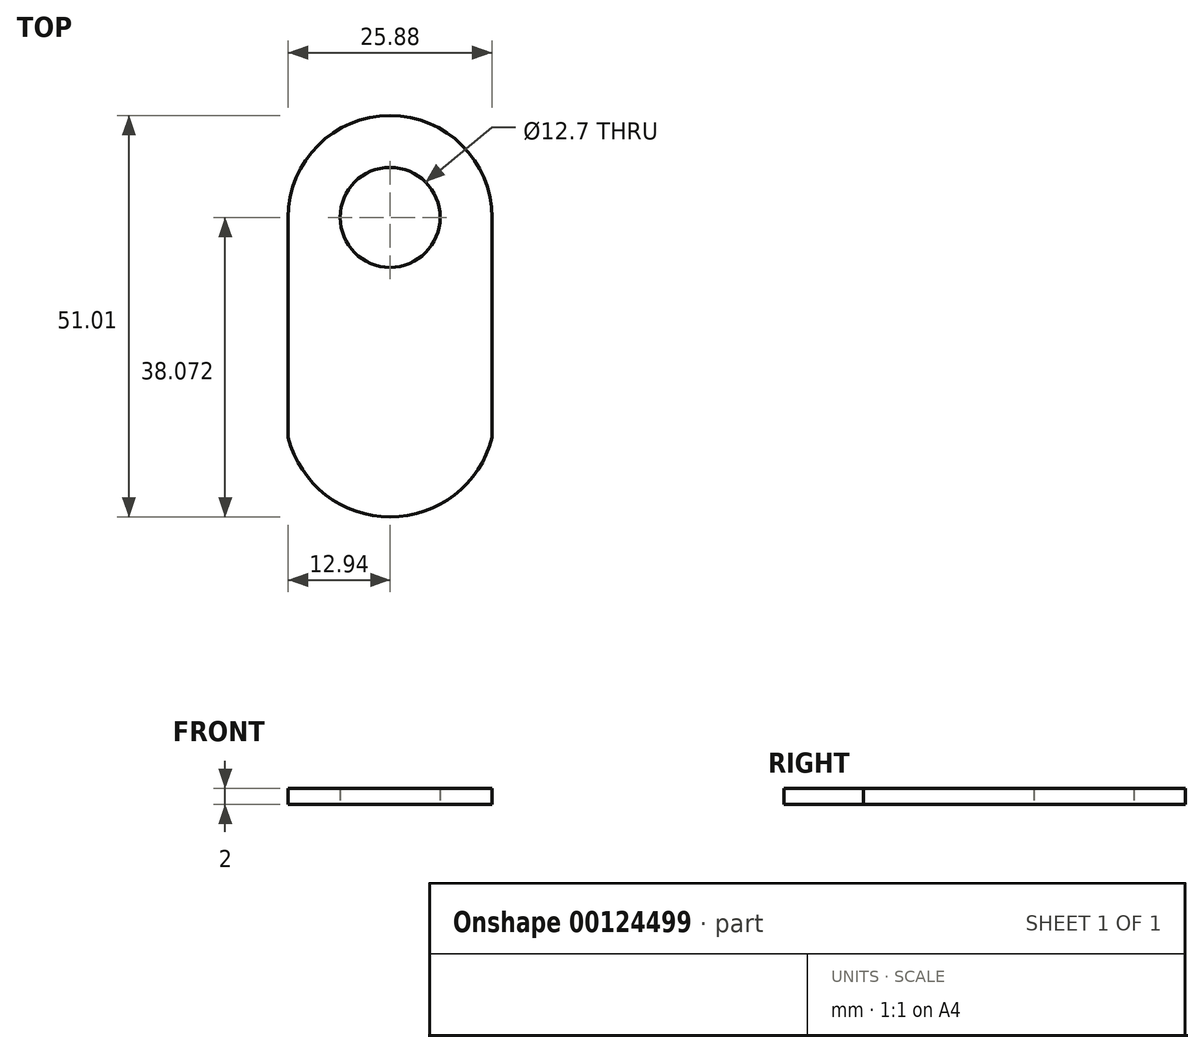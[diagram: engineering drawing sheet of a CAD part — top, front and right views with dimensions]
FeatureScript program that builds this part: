
annotation { "Feature Type Name" : "Feature", "Feature Type Description" : "" }
export const myFeature = defineFeature(function(context is Context, id is Id, definition is map)
    precondition{}
    {
        {
            var Q0;
            Q0=qCreatedBy(makeId("Top.planeOp"),FACE);
            var sketch = newSketch(context, id + "F0", { "sketchPlane" : qUnion([Q0])});
            skArc(sketch, "E0", {"start": v(-12.94, 0) * mm, "mid": v(0, -10.09) * mm, "end": v(12.94, 0) * mm});
            skLineSegment(sketch, "E1", {"start": v(-12.94, 0) * mm, "end": v(-12.94, 27.98) * mm});
            skLineSegment(sketch, "E2", {"start": v(12.94, 0) * mm, "end": v(12.94, 27.98) * mm});
            skArc(sketch, "E3", {"start": v(12.94, 27.98) * mm, "mid": v(0, 40.92) * mm, "end": v(-12.94, 27.98) * mm});
            skPoint(sketch, "E4", {"position": v(0, 0) * mm});
            skSolve(sketch);
        }
        {
            var Q0;
            Q0 = qSketchRegion(id + "F0", true);
            extrude(context, id + "F1", {"entities" : qUnion([Q0]), "depth" : 2 * mm});
        }
        {
            var Q0;
            Q0=sQuery(id+"F0.wireOp",VERTEX,"E3.center");
            var Q1;
            Q1=makeQuery(id+"F1.opExtrude","SWEPT_BODY",BODY,{"disambiguationData":[OSD([sQuery(id+"F0.wireOp",EDGE,"E0"),sQuery(id+"F0.wireOp",EDGE,"E1"),sQuery(id+"F0.wireOp",EDGE,"E2"),sQuery(id+"F0.wireOp",EDGE,"E3")])]});
            hole(context, id + "F2", {"style" : HoleStyle.SIMPLE, "endStyle" : HoleEndStyle.THROUGH, "oppositeDirection" : true, "holeDiameter" : 12.7 * mm, "locations" : qUnion([Q0]), "scope" : qUnion([Q1]), "isTappedThrough" : true});
        }
    });
